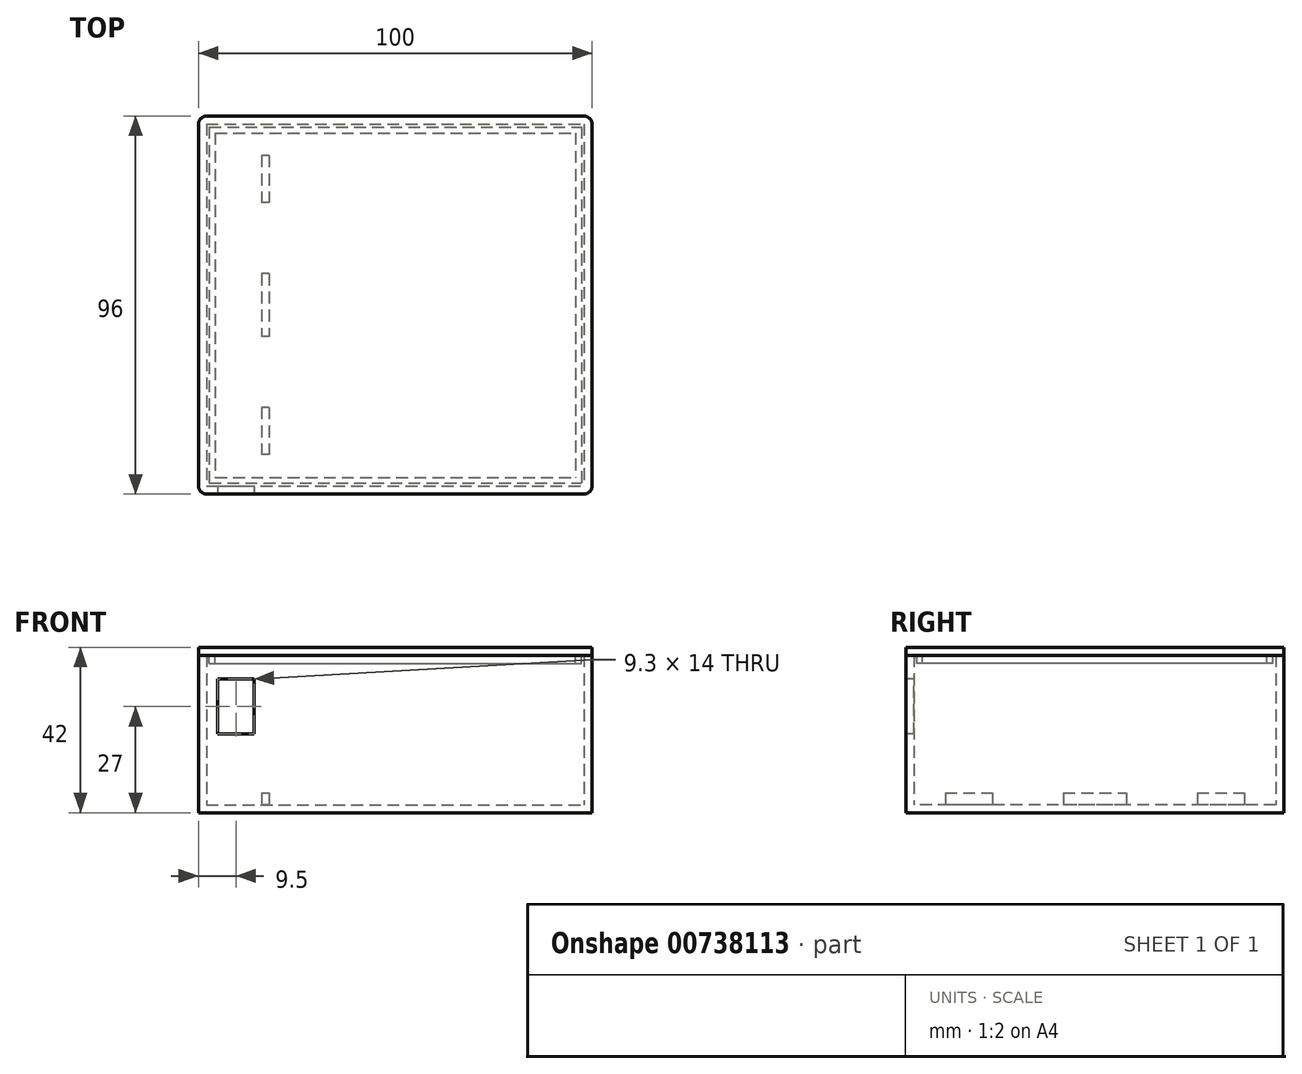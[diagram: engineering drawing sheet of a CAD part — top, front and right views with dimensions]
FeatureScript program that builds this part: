
annotation { "Feature Type Name" : "Feature", "Feature Type Description" : "" }
export const myFeature = defineFeature(function(context is Context, id is Id, definition is map)
    precondition{}
    {
        {
            var Q0;
            Q0=qCreatedBy(makeId("Top.planeOp"),FACE);
            var sketch = newSketch(context, id + "F0", { "sketchPlane" : qUnion([Q0])});
            skLineSegment(sketch, "E0.bottom", {"start": v(-50, 48) * mm, "end": v(50, 48) * mm});
            skLineSegment(sketch, "E0.top", {"start": v(-50, -48) * mm, "end": v(50, -48) * mm});
            skLineSegment(sketch, "E0.left", {"start": v(-50, 48) * mm, "end": v(-50, -48) * mm});
            skLineSegment(sketch, "E0.right", {"start": v(50, 48) * mm, "end": v(50, -48) * mm});
            skPoint(sketch, "E0.middle", {"position": v(0, 0) * mm});
            skSolve(sketch);
        }
        {
            var Q0;
            Q0=makeQuery(id+"F0.imprint","IMPRINT",FACE,{"disambiguationData":[TD([[makeQuery(id+"F0.imprint","IMPRINT",EDGE,{"derivedFrom":sQuery(id+"F0.wireOp",EDGE,"E0.bottom")}),-1.0]])]});
            extrude(context, id + "F1", {"entities" : qUnion([Q0]), "depth" : 40 * mm, "offsetDistance" : 25 * mm});
        }
        {
            var Q0;
            Q0=makeQuery(id+"F1.opExtrude","CAP_FACE",FACE,{"disambiguationData":[OSD([sQuery(id+"F0.wireOp",EDGE,"E0.bottom"),sQuery(id+"F0.wireOp",EDGE,"E0.top"),sQuery(id+"F0.wireOp",EDGE,"E0.left"),sQuery(id+"F0.wireOp",EDGE,"E0.right")])],"isStart":false});
            shell(context, id + "F2", {"entities" : qUnion([Q0]), "thickness" : 2 * mm});
        }
        {
            var Q0;
            Q0=makeQuery(id+"F1.opExtrude","SWEPT_FACE",FACE,{"disambiguationData":[OSD([sQuery(id+"F0.wireOp",EDGE,"E0.top")])]});
            var sketch = newSketch(context, id + "F3", { "sketchPlane" : qUnion([Q0])});
            skLineSegment(sketch, "E1", {"start": v(-31, 40) * mm, "end": v(-31, 0) * mm, "construction": true});
            skLineSegment(sketch, "E2.bottom", {"start": v(-45.15, 20) * mm, "end": v(-35.85, 20) * mm});
            skLineSegment(sketch, "E2.top", {"start": v(-45.15, 34) * mm, "end": v(-35.85, 34) * mm});
            skLineSegment(sketch, "E2.left", {"start": v(-45.15, 20) * mm, "end": v(-45.15, 34) * mm});
            skLineSegment(sketch, "E2.right", {"start": v(-35.85, 20) * mm, "end": v(-35.85, 34) * mm});
            skPoint(sketch, "E2.middle", {"position": v(-40.5, 27) * mm});
            skSolve(sketch);
        }
        {
            var Q0;
            Q0=makeQuery(id+"F3.imprint","IMPRINT",FACE,{"disambiguationData":[TD([[makeQuery(id+"F3.imprint","IMPRINT",EDGE,{"derivedFrom":sQuery(id+"F3.wireOp",EDGE,"E2.bottom")}),1.0]])]});
            var Q1;
            Q1=makeQuery(id+"F3.imprint","IMPRINT",FACE,{"disambiguationData":[TD([[makeQuery(id+"F3.imprint","IMPRINT",EDGE,{"derivedFrom":sQuery(id+"F3.wireOp",EDGE,"inGzHBys-gX4W-uZWt-QDCV-WMzDjeumildE")}),1.0]])]});
            extrude(context, id + "F4", {"entities" : qUnion([Q0, Q1]), "operationType" : NewBodyOperationType.REMOVE, "endBound" : BoundingType.UP_TO_NEXT, "oppositeDirection" : true, "depth" : 25 * mm, "offsetDistance" : 25 * mm});
        }
        {
            var Q0;
            Q0=makeQuery(id+"F1.opExtrude","CAP_FACE",FACE,{"disambiguationData":[OSD([sQuery(id+"F0.wireOp",EDGE,"E0.bottom"),sQuery(id+"F0.wireOp",EDGE,"E0.top"),sQuery(id+"F0.wireOp",EDGE,"E0.left"),sQuery(id+"F0.wireOp",EDGE,"E0.right")])],"isStart":true});
            var sketch = newSketch(context, id + "F5", { "sketchPlane" : qUnion([Q0])});
            skLineSegment(sketch, "E3.left", {"start": v(-32, 38) * mm, "end": v(-32, 26) * mm});
            skLineSegment(sketch, "E3.right", {"start": v(-34, 38) * mm, "end": v(-34, 26) * mm});
            skLineSegment(sketch, "E4", {"start": v(-34, 38) * mm, "end": v(-32, 38) * mm});
            skLineSegment(sketch, "E5", {"start": v(-34, 26) * mm, "end": v(-32, 26) * mm});
            skLineSegment(sketch, "E6", {"start": v(-34, 8) * mm, "end": v(-32, 8) * mm});
            skLineSegment(sketch, "E7.trimOffspring", {"start": v(-32, 8) * mm, "end": v(-32, -8) * mm});
            skLineSegment(sketch, "E8.trimOffspring", {"start": v(-34, 8) * mm, "end": v(-34, -8) * mm});
            skLineSegment(sketch, "E9.MirrorCS", {"start": v(-34, -38) * mm, "end": v(-32, -38) * mm});
            skLineSegment(sketch, "E10.MirrorCS", {"start": v(-34, -26) * mm, "end": v(-32, -26) * mm});
            skLineSegment(sketch, "E11.MirrorCS", {"start": v(-34, -8) * mm, "end": v(-32, -8) * mm});
            skLineSegment(sketch, "E12.trimOffspring", {"start": v(-32, -26) * mm, "end": v(-32, -38) * mm});
            skLineSegment(sketch, "E13.trimOffspring", {"start": v(-34, -26) * mm, "end": v(-34, -38) * mm});
            skSolve(sketch);
        }
        {
            var Q0;
            Q0=makeQuery(id+"F5.imprint","IMPRINT",FACE,{"disambiguationData":[TD([[makeQuery(id+"F5.imprint","IMPRINT",EDGE,{"derivedFrom":sQuery(id+"F5.wireOp",EDGE,"E3.left")}),-1.0]])]});
            var Q1;
            Q1=makeQuery(id+"F5.imprint","IMPRINT",FACE,{"disambiguationData":[TD([[makeQuery(id+"F5.imprint","IMPRINT",EDGE,{"derivedFrom":sQuery(id+"F5.wireOp",EDGE,"E6")}),-1.0]])]});
            var Q2;
            Q2=makeQuery(id+"F5.imprint","IMPRINT",FACE,{"disambiguationData":[TD([[makeQuery(id+"F5.imprint","IMPRINT",EDGE,{"derivedFrom":sQuery(id+"F5.wireOp",EDGE,"E9.MirrorCS")}),1.0]])]});
            extrude(context, id + "F6", {"entities" : qUnion([Q0, Q1, Q2]), "operationType" : NewBodyOperationType.ADD, "oppositeDirection" : true, "depth" : 5 * mm, "offsetDistance" : 25 * mm});
        }
        {
            var Q0;
            Q0=makeQuery(id+"F1.opExtrude","SWEPT_EDGE",EDGE,{"disambiguationData":[OSD([sQuery(id+"F0.wireOp",EDGE,"E0.top"),sQuery(id+"F0.wireOp",EDGE,"E0.left")])]});
            var Q1;
            Q1=makeQuery(id+"F1.opExtrude","SWEPT_EDGE",EDGE,{"disambiguationData":[OSD([sQuery(id+"F0.wireOp",EDGE,"E0.top"),sQuery(id+"F0.wireOp",EDGE,"E0.right")])]});
            var Q2;
            Q2=makeQuery(id+"F1.opExtrude","SWEPT_EDGE",EDGE,{"disambiguationData":[OSD([sQuery(id+"F0.wireOp",EDGE,"E0.bottom"),sQuery(id+"F0.wireOp",EDGE,"E0.right")])]});
            var Q3;
            Q3=makeQuery(id+"F1.opExtrude","SWEPT_EDGE",EDGE,{"disambiguationData":[OSD([sQuery(id+"F0.wireOp",EDGE,"E0.bottom"),sQuery(id+"F0.wireOp",EDGE,"E0.left")])]});
            fillet(context, id + "F7", {"entities" : qUnion([Q0, Q1, Q2, Q3]), "radius" : 2 * mm, "tangentPropagation" : true, "allowEdgeOverflow" : false});
        }
        {
            var Q0;
            Q0=makeQuery(id+"F1.opExtrude","CAP_FACE",FACE,{"disambiguationData":[OSD([sQuery(id+"F0.wireOp",EDGE,"E0.bottom"),sQuery(id+"F0.wireOp",EDGE,"E0.top"),sQuery(id+"F0.wireOp",EDGE,"E0.left"),sQuery(id+"F0.wireOp",EDGE,"E0.right")])],"isStart":false});
            var sketch = newSketch(context, id + "F8", { "sketchPlane" : qUnion([Q0])});
            skPoint(sketch, "E14.middle", {"position": v(0, 0) * mm});
            skLineSegment(sketch, "E15.bottom", {"start": v(-47.25, 45.25) * mm, "end": v(47.25, 45.25) * mm});
            skLineSegment(sketch, "E15.top", {"start": v(-47.25, -45.25) * mm, "end": v(47.25, -45.25) * mm});
            skLineSegment(sketch, "E15.left", {"start": v(-47.25, 45.25) * mm, "end": v(-47.25, -45.25) * mm});
            skLineSegment(sketch, "E15.right", {"start": v(47.25, 45.25) * mm, "end": v(47.25, -45.25) * mm});
            skLineSegment(sketch, "E16.bottom", {"start": v(-45.75, 43.75) * mm, "end": v(45.75, 43.75) * mm});
            skLineSegment(sketch, "E16.top", {"start": v(-45.75, -43.75) * mm, "end": v(45.75, -43.75) * mm});
            skLineSegment(sketch, "E16.left", {"start": v(-45.75, 43.75) * mm, "end": v(-45.75, -43.75) * mm});
            skLineSegment(sketch, "E16.right", {"start": v(45.75, 43.75) * mm, "end": v(45.75, -43.75) * mm});
            skSolve(sketch);
        }
        {
            var Q0;
            {var subQ3=sQuery(id+"F0.wireOp",EDGE,"E0.bottom");Q0=makeQuery(id+"F8.imprint","IMPRINT",FACE,{"disambiguationData":[TD([[makeQuery(id+"F8.imprint","IMPRINT",EDGE,{"derivedFrom":makeQuery(id+"F2.opShell","OFFSET_EDGE",EDGE,{"disambiguationData":[OSD([subQ3]),TDD([makeQuery(id+"F1.opExtrude","CAP_EDGE",EDGE,{"disambiguationData":[OSD([subQ3])],"isStart":false})])]})}),1.0]])]});}
            var sketch = newSketch(context, id + "F9", { "sketchPlane" : qUnion([Q0])});
            skLineSegment(sketch, "E17.bottom", {"start": v(-50, 48) * mm, "end": v(50, 48) * mm});
            skLineSegment(sketch, "E17.top", {"start": v(-50, -48) * mm, "end": v(50, -48) * mm});
            skLineSegment(sketch, "E17.left", {"start": v(-50, 48) * mm, "end": v(-50, -48) * mm});
            skLineSegment(sketch, "E17.right", {"start": v(50, 48) * mm, "end": v(50, -48) * mm});
            skPoint(sketch, "E17.middle", {"position": v(0, 0) * mm});
            skSolve(sketch);
        }
        {
            var Q0;
            Q0 = qSketchRegion(id + "F9", true);
            extrude(context, id + "F10", {"entities" : qUnion([Q0]), "depth" : 2 * mm, "offsetDistance" : 25 * mm});
        }
        {
            var Q0;
            Q0 = qSketchRegion(id + "F8", true);
            extrude(context, id + "F11", {"entities" : qUnion([Q0]), "operationType" : NewBodyOperationType.ADD, "oppositeDirection" : true, "depth" : 2 * mm, "offsetDistance" : 25 * mm});
        }
        {
            var Q0;
            Q0=makeQuery(id+"F10.opExtrude","SWEPT_EDGE",EDGE,{"disambiguationData":[OSD([sQuery(id+"F9.wireOp",EDGE,"E17.top"),sQuery(id+"F9.wireOp",EDGE,"E17.left")])]});
            var Q1;
            Q1=makeQuery(id+"F10.opExtrude","SWEPT_EDGE",EDGE,{"disambiguationData":[OSD([sQuery(id+"F9.wireOp",EDGE,"E17.top"),sQuery(id+"F9.wireOp",EDGE,"E17.right")])]});
            var Q2;
            Q2=makeQuery(id+"F10.opExtrude","SWEPT_EDGE",EDGE,{"disambiguationData":[OSD([sQuery(id+"F9.wireOp",EDGE,"E17.bottom"),sQuery(id+"F9.wireOp",EDGE,"E17.right")])]});
            var Q3;
            Q3=makeQuery(id+"F10.opExtrude","SWEPT_EDGE",EDGE,{"disambiguationData":[OSD([sQuery(id+"F9.wireOp",EDGE,"E17.bottom"),sQuery(id+"F9.wireOp",EDGE,"E17.left")])]});
            fillet(context, id + "F12", {"entities" : qUnion([Q0, Q1, Q2, Q3]), "radius" : 2 * mm, "tangentPropagation" : true, "allowEdgeOverflow" : false});
        }
    });
